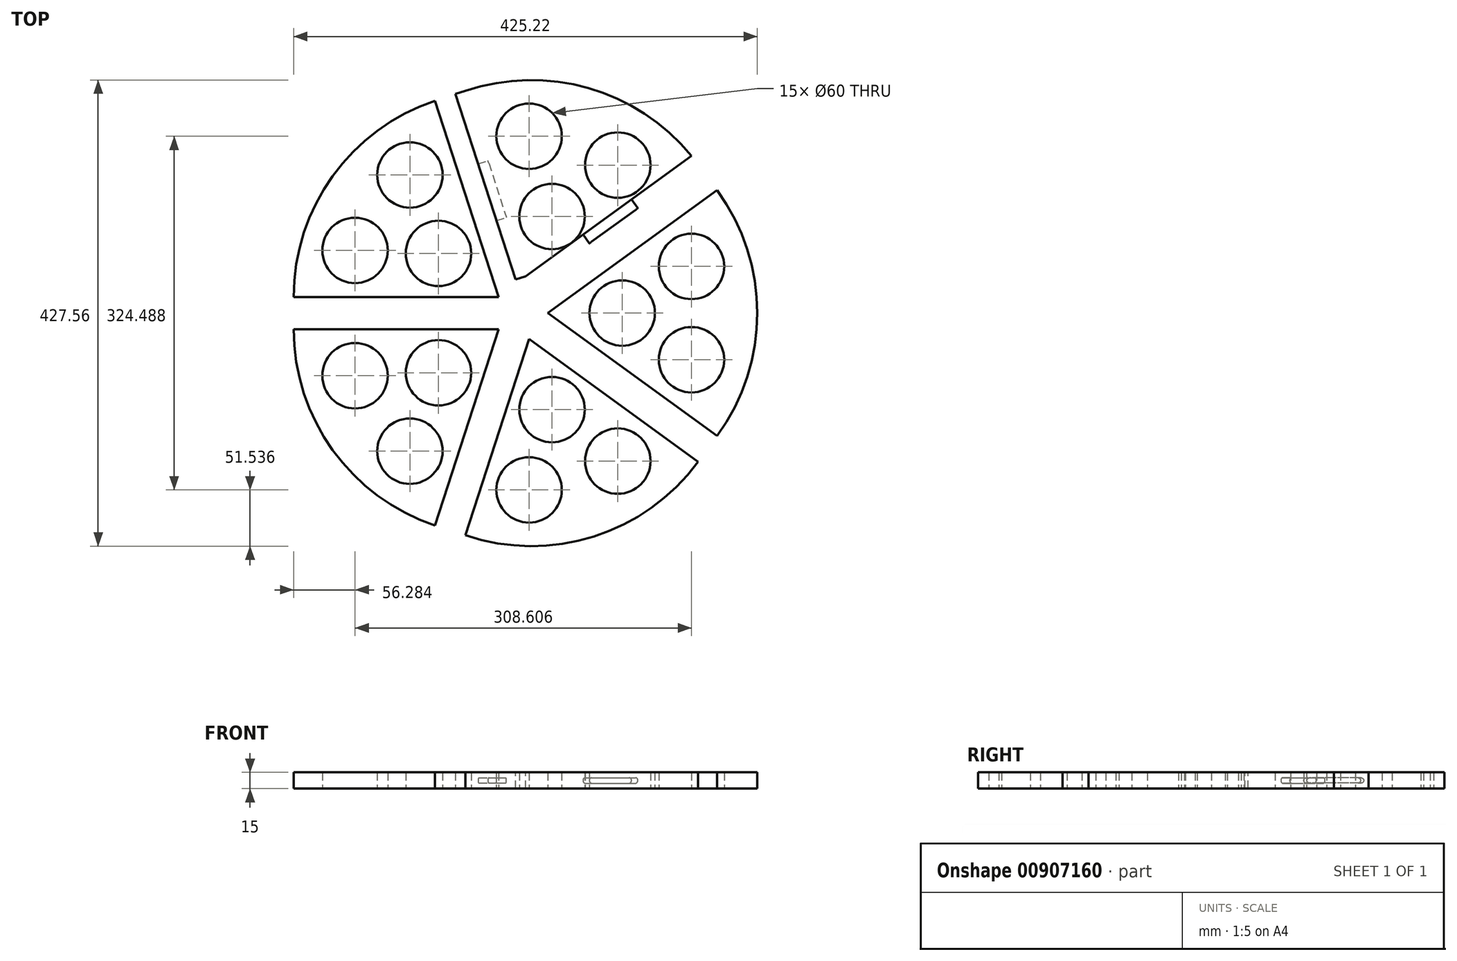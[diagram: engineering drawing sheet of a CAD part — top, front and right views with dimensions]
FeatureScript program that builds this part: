
annotation { "Feature Type Name" : "Feature", "Feature Type Description" : "" }
export const myFeature = defineFeature(function(context is Context, id is Id, definition is map)
    precondition{}
    {
        {
            var Q0;
            Q0=qCreatedBy(makeId("Top.planeOp"),FACE);
            var sketch = newSketch(context, id + "F0", { "sketchPlane" : qUnion([Q0])});
            skCircle(sketch, "E0", {"center": v(2.02, 0) * mm, "radius": 190 * mm});
            skCircle(sketch, "E1", {"center": v(0, 138.47) * mm, "radius": 30 * mm});
            skCircle(sketch, "E2.1.0", {"center": v(-81.39, 112.02) * mm, "radius": 30 * mm});
            skCircle(sketch, "E2.2.0", {"center": v(-131.7, 42.79) * mm, "radius": 30 * mm});
            skCircle(sketch, "E2.3.0", {"center": v(-131.7, -42.79) * mm, "radius": 30 * mm});
            skCircle(sketch, "E2.4.0", {"center": v(-81.39, -112.02) * mm, "radius": 30 * mm});
            skCircle(sketch, "E2.5.0", {"center": v(0, -138.47) * mm, "radius": 30 * mm});
            skCircle(sketch, "E2.6.0", {"center": v(81.39, -112.02) * mm, "radius": 30 * mm});
            skCircle(sketch, "E2.7.0", {"center": v(131.7, -42.79) * mm, "radius": 30 * mm});
            skCircle(sketch, "E2.8.0", {"center": v(131.7, 42.79) * mm, "radius": 30 * mm});
            skCircle(sketch, "E2.9.0", {"center": v(81.39, 112.02) * mm, "radius": 30 * mm});
            skPoint(sketch, "E2.center", {"position": v(0, 0) * mm});
            skCircle(sketch, "E3", {"center": v(21.05, 64.8) * mm, "radius": 30 * mm});
            skCircle(sketch, "E4.1.0", {"center": v(-55.12, 40.05) * mm, "radius": 30 * mm});
            skCircle(sketch, "E4.2.0", {"center": v(-55.12, -40.05) * mm, "radius": 30 * mm});
            skCircle(sketch, "E4.3.0", {"center": v(21.05, -64.8) * mm, "radius": 30 * mm});
            skCircle(sketch, "E4.4.0", {"center": v(68.13, 0) * mm, "radius": 30 * mm});
            skLineSegment(sketch, "E5", {"start": v(0, 138.47) * mm, "end": v(81.39, 112.02) * mm, "construction": true});
            skLineSegment(sketch, "E6", {"start": v(-81.39, -112.02) * mm, "end": v(0, -138.47) * mm, "construction": true});
            skLineSegment(sketch, "E7", {"start": v(-40.7, -125.25) * mm, "end": v(40.7, 125.25) * mm, "construction": true});
            skLineSegment(sketch, "E8", {"start": v(0, 138.47) * mm, "end": v(-81.39, 112.02) * mm, "construction": true});
            skLineSegment(sketch, "E9", {"start": v(-131.7, 42.79) * mm, "end": v(-131.7, -42.79) * mm, "construction": true});
            skLineSegment(sketch, "E10", {"start": v(81.39, -112.02) * mm, "end": v(131.7, -42.79) * mm, "construction": true});
            skLineSegment(sketch, "E11", {"start": v(0, 0) * mm, "end": v(-61.47, 189.17) * mm});
            skLineSegment(sketch, "E12", {"start": v(0, 0) * mm, "end": v(-64.77, -199.33) * mm});
            skLineSegment(sketch, "E13", {"start": v(0, 0) * mm, "end": v(167.22, -121.5) * mm});
            skLineSegment(sketch, "E14", {"start": v(0, 0) * mm, "end": v(-204.97, 0) * mm});
            skPoint(sketch, "E14.endSnap0", {"position": v(-131.7, 0) * mm});
            skLineSegment(sketch, "E15", {"start": v(131.7, 42.79) * mm, "end": v(81.39, 112.02) * mm, "construction": true});
            skLineSegment(sketch, "E16", {"start": v(0, 0) * mm, "end": v(170.16, 123.63) * mm});
            skSolve(sketch);
        }
        {
            var Q0;
            Q0=makeQuery(id+"F0.imprint","IMPRINT",FACE,{"disambiguationData":[TD([[makeQuery(id+"F0.imprint","IMPRINT",EDGE,{"derivedFrom":sQuery(id+"F0.wireOp",EDGE,"E1")}),-1.0]])]});
            extrude(context, id + "F1", {"entities" : qUnion([Q0]), "depth" : 15 * mm, "offsetDistance" : 25 * mm});
        }
        {
            var Q0;
            Q0=makeQuery(id+"F0.imprint","IMPRINT",FACE,{"disambiguationData":[TD([[makeQuery(id+"F0.imprint","IMPRINT",EDGE,{"derivedFrom":sQuery(id+"F0.wireOp",EDGE,"E2.1.0")}),-1.0]])]});
            extrude(context, id + "F2", {"entities" : qUnion([Q0]), "depth" : 15 * mm, "offsetDistance" : 25 * mm});
        }
        {
            var Q0;
            Q0=makeQuery(id+"F0.imprint","IMPRINT",FACE,{"disambiguationData":[TD([[makeQuery(id+"F0.imprint","IMPRINT",EDGE,{"derivedFrom":sQuery(id+"F0.wireOp",EDGE,"E2.3.0")}),-1.0]])]});
            extrude(context, id + "F3", {"entities" : qUnion([Q0]), "depth" : 15 * mm, "offsetDistance" : 25 * mm});
        }
        {
            var Q0;
            Q0=makeQuery(id+"F0.imprint","IMPRINT",FACE,{"disambiguationData":[TD([[makeQuery(id+"F0.imprint","IMPRINT",EDGE,{"derivedFrom":sQuery(id+"F0.wireOp",EDGE,"E2.5.0")}),-1.0]])]});
            extrude(context, id + "F4", {"entities" : qUnion([Q0]), "depth" : 15 * mm, "offsetDistance" : 25 * mm});
        }
        {
            var Q0;
            Q0=makeQuery(id+"F0.imprint","IMPRINT",FACE,{"disambiguationData":[TD([[makeQuery(id+"F0.imprint","IMPRINT",EDGE,{"derivedFrom":sQuery(id+"F0.wireOp",EDGE,"E2.7.0")}),-1.0]])]});
            extrude(context, id + "F5", {"entities" : qUnion([Q0]), "depth" : 15 * mm, "offsetDistance" : 25 * mm});
        }
        {
            var Q0;
            Q0=makeQuery(id+"F1.opExtrude","SWEPT_BODY",BODY,{"disambiguationData":[OSD([sQuery(id+"F0.wireOp",EDGE,"E0"),sQuery(id+"F0.wireOp",EDGE,"E1"),sQuery(id+"F0.wireOp",EDGE,"E2.9.0"),sQuery(id+"F0.wireOp",EDGE,"E3"),sQuery(id+"F0.wireOp",EDGE,"E11"),sQuery(id+"F0.wireOp",EDGE,"E16")])]});
            var Q1;
            Q1=sQuery(id+"F0.wireOp",EDGE,"E7");
            var Q2;
            Q2=sQuery(id+"F0.wireOp",EDGE,"E7");
            transform(context, id + "F6", {"entities" : qUnion([Q0]), "transformType" : TransformType.TRANSLATION_DISTANCE, "transformDirection" : qUnion([Q2]), "distance" : 25 * mm, "makeCopy" : false});
        }
        {
            var Q0;
            Q0=makeQuery(id+"F2.opExtrude","SWEPT_BODY",BODY,{"disambiguationData":[OSD([sQuery(id+"F0.wireOp",EDGE,"E0"),sQuery(id+"F0.wireOp",EDGE,"E2.1.0"),sQuery(id+"F0.wireOp",EDGE,"E2.2.0"),sQuery(id+"F0.wireOp",EDGE,"E4.1.0"),sQuery(id+"F0.wireOp",EDGE,"E11"),sQuery(id+"F0.wireOp",EDGE,"E14")])]});
            var Q1;
            Q1=sQuery(id+"F0.wireOp",EDGE,"E13");
            transform(context, id + "F7", {"entities" : qUnion([Q0]), "transformType" : TransformType.TRANSLATION_DISTANCE, "transformDirection" : qUnion([Q1]), "distance" : 25 * mm, "oppositeDirection" : true, "makeCopy" : false});
        }
        {
            var Q0;
            Q0=makeQuery(id+"F3.opExtrude","SWEPT_BODY",BODY,{"disambiguationData":[OSD([sQuery(id+"F0.wireOp",EDGE,"E0"),sQuery(id+"F0.wireOp",EDGE,"E2.3.0"),sQuery(id+"F0.wireOp",EDGE,"E2.4.0"),sQuery(id+"F0.wireOp",EDGE,"E4.2.0"),sQuery(id+"F0.wireOp",EDGE,"E12"),sQuery(id+"F0.wireOp",EDGE,"E14")])]});
            var Q1;
            Q1=sQuery(id+"F0.wireOp",EDGE,"E16");
            transform(context, id + "F8", {"entities" : qUnion([Q0]), "transformType" : TransformType.TRANSLATION_DISTANCE, "transformDirection" : qUnion([Q1]), "distance" : 25 * mm, "oppositeDirection" : true, "makeCopy" : false});
        }
        {
            var Q0;
            Q0=makeQuery(id+"F4.opExtrude","SWEPT_BODY",BODY,{"disambiguationData":[OSD([sQuery(id+"F0.wireOp",EDGE,"E0"),sQuery(id+"F0.wireOp",EDGE,"E2.5.0"),sQuery(id+"F0.wireOp",EDGE,"E2.6.0"),sQuery(id+"F0.wireOp",EDGE,"E4.3.0"),sQuery(id+"F0.wireOp",EDGE,"E12"),sQuery(id+"F0.wireOp",EDGE,"E13")])]});
            var Q1;
            Q1=sQuery(id+"F0.wireOp",EDGE,"E11");
            transform(context, id + "F9", {"entities" : qUnion([Q0]), "transformType" : TransformType.TRANSLATION_DISTANCE, "transformDirection" : qUnion([Q1]), "distance" : 25 * mm, "oppositeDirection" : true, "makeCopy" : false});
        }
        {
            var Q0;
            Q0=makeQuery(id+"F5.opExtrude","SWEPT_BODY",BODY,{"disambiguationData":[OSD([sQuery(id+"F0.wireOp",EDGE,"E0"),sQuery(id+"F0.wireOp",EDGE,"E2.7.0"),sQuery(id+"F0.wireOp",EDGE,"E2.8.0"),sQuery(id+"F0.wireOp",EDGE,"E4.4.0"),sQuery(id+"F0.wireOp",EDGE,"E13"),sQuery(id+"F0.wireOp",EDGE,"E16")])]});
            var Q1;
            Q1=sQuery(id+"F0.wireOp",EDGE,"E14");
            transform(context, id + "F10", {"entities" : qUnion([Q0]), "transformType" : TransformType.TRANSLATION_DISTANCE, "transformDirection" : qUnion([Q1]), "distance" : 25 * mm, "oppositeDirection" : true, "makeCopy" : false});
        }
        {
            var Q0;
            Q0=makeQuery(id+"F1.opExtrude","SWEPT_FACE",FACE,{"disambiguationData":[OSD([sQuery(id+"F0.wireOp",EDGE,"E16")])]});
            var sketch = newSketch(context, id + "F11", { "sketchPlane" : qUnion([Q0])});
            skLineSegment(sketch, "E17", {"start": v(116.04, 0) * mm, "end": v(116.04, 15) * mm, "construction": true});
            skPoint(sketch, "E18.startSnap0", {"position": v(116.04, 7.5) * mm});
            skLineSegment(sketch, "E19", {"start": v(91.04, 7.5) * mm, "end": v(141.04, 7.5) * mm});
            skArc(sketch, "E20.0.startCap", {"start": v(91.04, 5) * mm, "mid": v(88.54, 7.5) * mm, "end": v(91.04, 10) * mm});
            skArc(sketch, "E20.0.endCap", {"start": v(141.04, 10) * mm, "mid": v(143.54, 7.5) * mm, "end": v(141.04, 5) * mm});
            skLineSegment(sketch, "E20.0.left", {"start": v(91.04, 10) * mm, "end": v(141.04, 10) * mm});
            skLineSegment(sketch, "E20.0.right", {"start": v(91.04, 5) * mm, "end": v(141.04, 5) * mm});
            skSolve(sketch);
        }
        {
            var Q0;
            Q0=makeQuery(id+"F11.imprint","IMPRINT",FACE,{"disambiguationData":[TD([[makeQuery(id+"F11.imprint","IMPRINT",EDGE,{"derivedFrom":sQuery(id+"F11.wireOp",EDGE,"E20.0.startCap")}),-1.0]])]});
            extrude(context, id + "F12", {"entities" : qUnion([Q0]), "operationType" : NewBodyOperationType.REMOVE, "oppositeDirection" : true, "depth" : 10 * mm, "offsetDistance" : 25 * mm});
        }
        {
            var Q0;
            Q0=makeQuery(id+"F1.opExtrude","SWEPT_FACE",FACE,{"disambiguationData":[OSD([sQuery(id+"F0.wireOp",EDGE,"E11")])]});
            var sketch = newSketch(context, id + "F13", { "sketchPlane" : qUnion([Q0])});
            skLineSegment(sketch, "E21", {"start": v(-114.9, 0) * mm, "end": v(-114.9, 15) * mm, "construction": true});
            skLineSegment(sketch, "E22", {"start": v(-139.9, 7.5) * mm, "end": v(-89.9, 7.5) * mm});
            skPoint(sketch, "E22.startSnap0", {"position": v(-114.9, 7.5) * mm});
            skArc(sketch, "E23.0.startCap", {"start": v(-139.9, 5.12) * mm, "mid": v(-142.28, 7.5) * mm, "end": v(-139.9, 9.88) * mm});
            skArc(sketch, "E23.0.endCap", {"start": v(-89.9, 9.88) * mm, "mid": v(-87.53, 7.5) * mm, "end": v(-89.9, 5.12) * mm});
            skLineSegment(sketch, "E23.0.left", {"start": v(-139.9, 9.88) * mm, "end": v(-89.9, 9.88) * mm});
            skLineSegment(sketch, "E23.0.right", {"start": v(-139.9, 5.12) * mm, "end": v(-89.9, 5.12) * mm});
            skSolve(sketch);
        }
        {
            var Q0;
            Q0=makeQuery(id+"F13.imprint","IMPRINT",FACE,{"disambiguationData":[TD([[makeQuery(id+"F13.imprint","IMPRINT",EDGE,{"derivedFrom":sQuery(id+"F13.wireOp",EDGE,"E23.0.startCap")}),-1.0]])]});
            extrude(context, id + "F14", {"entities" : qUnion([Q0]), "operationType" : NewBodyOperationType.ADD, "depth" : 9.5 * mm, "offsetDistance" : 25 * mm});
        }
    });
